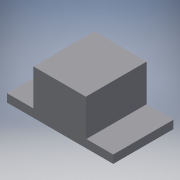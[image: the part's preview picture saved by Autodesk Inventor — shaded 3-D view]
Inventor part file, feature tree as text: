
AUTODESK INVENTOR PART (.ipt)
format: ipt  version: 2018 (Build 220112000, 112)  size: 103,936 bytes
history: native  units: mm
features: extrude x2, sketch x2
ambient origin geometry x8: Origin, YZ Plane, XZ Plane, XY Plane, X Axis, Y Axis, Z Axis, Center Point
bodies: Solid1 (feature_tree)
feature tree (4):
  extrude  "Extrusion1"  Depth=53.1mm
  extrude  "Extrusion2"  Depth=30.14mm
  sketch  "Sketch1"  dims[d0=26.55mm d1=53.1mm]
  sketch  "Sketch2"  dims[d2=15.07mm d3=30.14mm d4=4.05mm d5=0.0mm d6=13.125mm d7=26.25mm d8=18.45mm d9=0.0mm]
